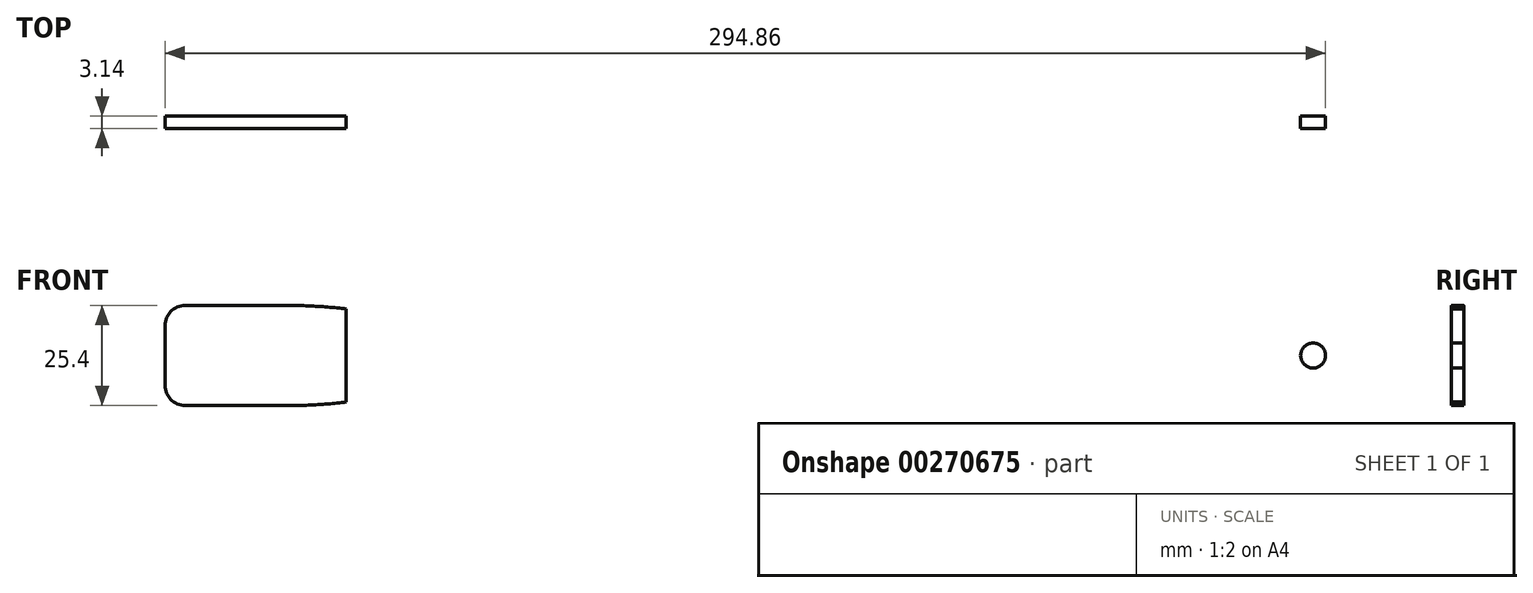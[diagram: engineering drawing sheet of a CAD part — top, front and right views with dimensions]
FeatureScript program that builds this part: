
annotation { "Feature Type Name" : "Feature", "Feature Type Description" : "" }
export const myFeature = defineFeature(function(context is Context, id is Id, definition is map)
    precondition{}
    {
        {
            var Q0;
            Q0=qCreatedBy(makeId("Front.planeOp"),FACE);
            var sketch = newSketch(context, id + "F0", { "sketchPlane" : qUnion([Q0])});
            skLineSegment(sketch, "E0.bottom", {"start": v(148.59, 12.7) * mm, "end": v(-71.29, 12.7) * mm});
            skLineSegment(sketch, "E0.top", {"start": v(148.59, -12.7) * mm, "end": v(-71.29, -12.7) * mm});
            skLineSegment(sketch, "E0.left", {"start": v(152.4, 8.9) * mm, "end": v(152.4, -8.9) * mm});
            skLineSegment(sketch, "E0.right", {"start": v(-152.4, 7.62) * mm, "end": v(-152.4, -7.62) * mm});
            skPoint(sketch, "E0.middle", {"position": v(0, 0) * mm});
            skFitSpline(sketch, "E1", {"points": [v(-120.32, 12.7) * mm, v(-71.29, 12.7) * mm], "startDerivative": vector(61.96, 0) * mm, "endDerivative": vector(32.49, 20.05) * mm});
            skLineSegment(sketch, "E2", {"start": v(0, 0) * mm, "end": v(-152.4, 0) * mm, "construction": true});
            skFitSpline(sketch, "E3.MirrorCS", {"points": [v(-120.32, -12.7) * mm, v(-71.29, -12.7) * mm], "startDerivative": vector(61.96, 0) * mm, "endDerivative": vector(32.49, -20.05) * mm});
            skPoint(sketch, "E4.visualSharp", {"position": v(-152.4, 12.7) * mm});
            skArc(sketch, "E4.filletArc", {"start": v(-147.32, 12.7) * mm, "mid": v(-150.91, 11.21) * mm, "end": v(-152.4, 7.62) * mm});
            skPoint(sketch, "E5.visualSharp", {"position": v(-152.4, -12.7) * mm});
            skArc(sketch, "E5.filletArc", {"start": v(-152.4, -7.62) * mm, "mid": v(-150.91, -11.21) * mm, "end": v(-147.32, -12.7) * mm});
            skPoint(sketch, "E6.visualSharp", {"position": v(152.4, 12.7) * mm});
            skArc(sketch, "E6.filletArc", {"start": v(152.4, 8.9) * mm, "mid": v(151.28, 11.58) * mm, "end": v(148.59, 12.7) * mm});
            skPoint(sketch, "E7.visualSharp", {"position": v(152.4, -12.7) * mm});
            skArc(sketch, "E7.filletArc", {"start": v(148.59, -12.7) * mm, "mid": v(151.28, -11.58) * mm, "end": v(152.4, -8.9) * mm});
            skLineSegment(sketch, "E8.trimOffspring", {"start": v(-120.32, 12.7) * mm, "end": v(-147.32, 12.7) * mm});
            skLineSegment(sketch, "E9.trimOffspring", {"start": v(-120.32, -12.7) * mm, "end": v(-147.32, -12.7) * mm});
            skLineSegment(sketch, "E10", {"start": v(-106.35, 11.86) * mm, "end": v(-106.35, -11.86) * mm});
            skSolve(sketch);
        }
        {
            var Q0;
            Q0=makeQuery(id+"F0.imprint","IMPRINT",FACE,{"disambiguationData":[TD([[makeQuery(id+"F0.imprint","IMPRINT",EDGE,{"derivedFrom":sQuery(id+"F0.wireOp",EDGE,"E0.bottom")}),1.0]])]});
            extrude(context, id + "F1", {"entities" : qUnion([Q0]), "endBound" : BoundingType.SYMMETRIC, "depth" : 3.15 * mm});
        }
        {
            var Q0;
            Q0=makeQuery(id+"F1.opExtrude","CAP_FACE",FACE,{"disambiguationData":[OSD([sQuery(id+"F0.wireOp",EDGE,"E0.bottom"),sQuery(id+"F0.wireOp",EDGE,"E0.top"),sQuery(id+"F0.wireOp",EDGE,"E0.left"),sQuery(id+"F0.wireOp",EDGE,"E0.right"),sQuery(id+"F0.wireOp",EDGE,"E1"),sQuery(id+"F0.wireOp",EDGE,"E3.MirrorCS"),sQuery(id+"F0.wireOp",EDGE,"E4.filletArc"),sQuery(id+"F0.wireOp",EDGE,"E5.filletArc"),sQuery(id+"F0.wireOp",EDGE,"E6.filletArc"),sQuery(id+"F0.wireOp",EDGE,"E7.filletArc"),sQuery(id+"F0.wireOp",EDGE,"E8.trimOffspring"),sQuery(id+"F0.wireOp",EDGE,"E9.trimOffspring")])],"isStart":false});
            var sketch = newSketch(context, id + "F2", { "sketchPlane" : qUnion([Q0])});
            skLineSegment(sketch, "E11", {"start": v(-50.8, 12.7) * mm, "end": v(-50.8, -12.7) * mm});
            skSolve(sketch);
        }
        {
            var Q0;
            {var subQ2=sQuery(id+"F2.wireOp",EDGE,"E11");Q0=makeQuery(id+"F2.imprint","IMPRINT",FACE,{"disambiguationData":[TD([[makeQuery(id+"F2.imprint","IMPRINT",EDGE,{"derivedFrom":subQ2}),-1.0]])]});}
            extrude(context, id + "F3", {"entities" : qUnion([Q0]), "operationType" : NewBodyOperationType.REMOVE, "oppositeDirection" : true, "depth" : 3.17 * mm});
        }
        {
            var Q0;
            Q0=makeQuery(id+"F1.opExtrude","CAP_FACE",FACE,{"disambiguationData":[OSD([sQuery(id+"F0.wireOp",EDGE,"E0.bottom"),sQuery(id+"F0.wireOp",EDGE,"E0.top"),sQuery(id+"F0.wireOp",EDGE,"E0.left"),sQuery(id+"F0.wireOp",EDGE,"E0.right"),sQuery(id+"F0.wireOp",EDGE,"E1"),sQuery(id+"F0.wireOp",EDGE,"E3.MirrorCS"),sQuery(id+"F0.wireOp",EDGE,"E4.filletArc"),sQuery(id+"F0.wireOp",EDGE,"E5.filletArc"),sQuery(id+"F0.wireOp",EDGE,"E6.filletArc"),sQuery(id+"F0.wireOp",EDGE,"E7.filletArc"),sQuery(id+"F0.wireOp",EDGE,"E8.trimOffspring"),sQuery(id+"F0.wireOp",EDGE,"E9.trimOffspring")])],"isStart":false});
            var sketch = newSketch(context, id + "F4", { "sketchPlane" : qUnion([Q0])});
            skLineSegment(sketch, "E12", {"start": v(48.9, 12.7) * mm, "end": v(48.9, -12.7) * mm, "construction": true});
            skLineSegment(sketch, "E13", {"start": v(48.9, 0) * mm, "end": v(-50.8, 0) * mm, "construction": true});
            skCircle(sketch, "E14", {"center": v(-41.5, 0) * mm, "radius": 3.18 * mm});
            skCircle(sketch, "E15.MirrorC", {"center": v(139.28, 0) * mm, "radius": 3.18 * mm});
            skCircle(sketch, "E16", {"center": v(100.03, 10.31) * mm, "radius": 1.27 * mm});
            skSolve(sketch);
        }
        {
            var Q0;
            Q0=makeQuery(id+"F4.imprint","IMPRINT",FACE,{"disambiguationData":[TD([[makeQuery(id+"F4.imprint","IMPRINT",EDGE,{"derivedFrom":sQuery(id+"F4.wireOp",EDGE,"E14")}),1.0]])]});
            var Q1;
            Q1=makeQuery(id+"F4.imprint","IMPRINT",FACE,{"disambiguationData":[TD([[makeQuery(id+"F4.imprint","IMPRINT",EDGE,{"derivedFrom":sQuery(id+"F4.wireOp",EDGE,"E15.MirrorC")}),-1.0]])]});
            var Q2;
            Q2=makeQuery(id+"F4.imprint","IMPRINT",FACE,{"disambiguationData":[TD([[makeQuery(id+"F4.imprint","IMPRINT",EDGE,{"derivedFrom":sQuery(id+"F4.wireOp",EDGE,"E16")}),1.0]])]});
            extrude(context, id + "F5", {"entities" : qUnion([Q0, Q1, Q2]), "operationType" : NewBodyOperationType.REMOVE, "oppositeDirection" : true, "depth" : 3.17 * mm});
        }
        {
            var Q0;
            Q0=makeQuery(id+"F0.imprint","IMPRINT",FACE,{"disambiguationData":[TD([[makeQuery(id+"F0.imprint","IMPRINT",EDGE,{"derivedFrom":sQuery(id+"F0.wireOp",EDGE,"E0.right")}),1.0]])]});
            extrude(context, id + "F6", {"entities" : qUnion([Q0]), "endBound" : BoundingType.SYMMETRIC, "depth" : 3.15 * mm});
        }
    });
